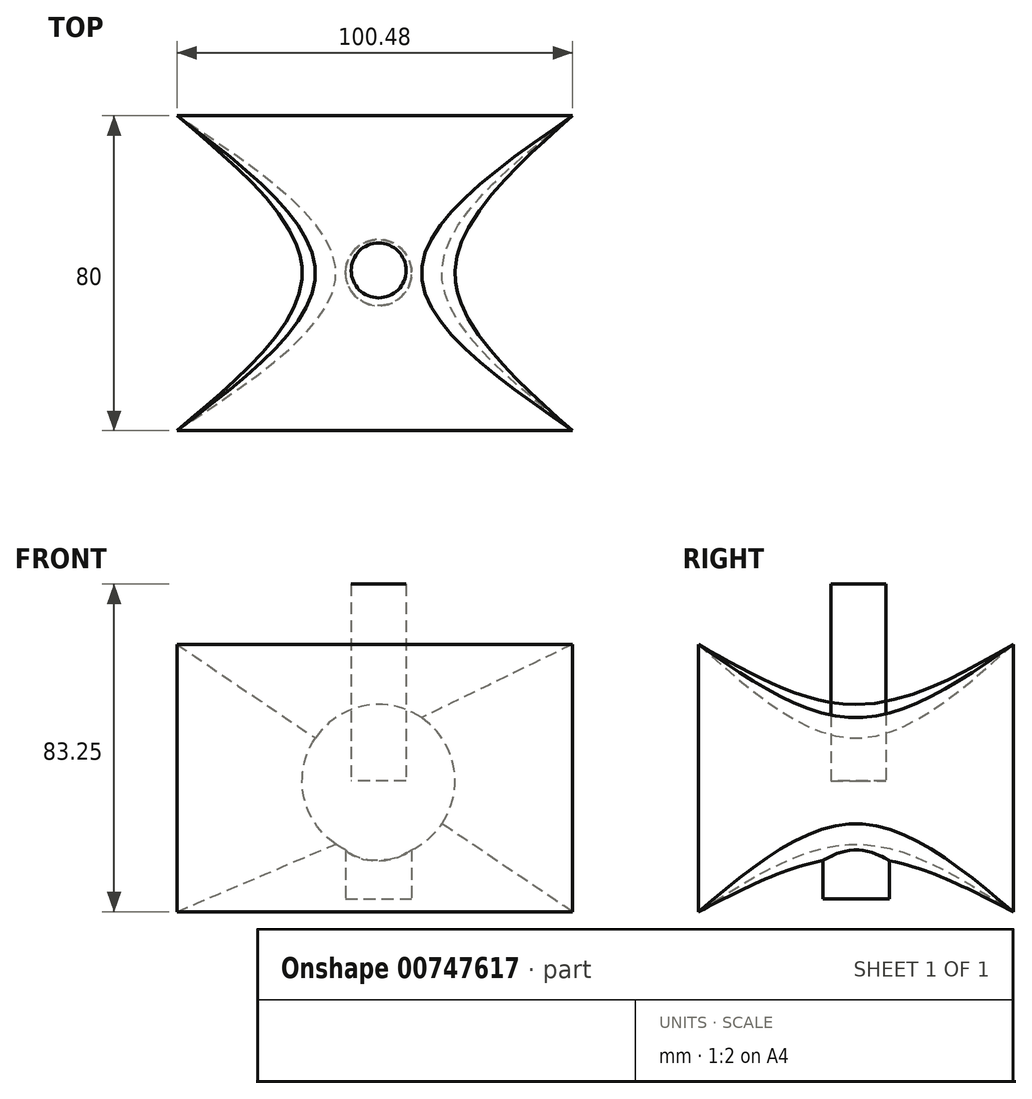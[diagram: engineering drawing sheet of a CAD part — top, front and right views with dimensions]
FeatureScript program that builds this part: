
annotation { "Feature Type Name" : "Feature", "Feature Type Description" : "" }
export const myFeature = defineFeature(function(context is Context, id is Id, definition is map)
    precondition{}
    {
        {
            var Q0;
            Q0=qCreatedBy(makeId("Front.planeOp"),FACE);
            var sketch = newSketch(context, id + "F0", { "sketchPlane" : qUnion([Q0])});
            skLineSegment(sketch, "E0.bottom", {"start": v(-51.24, 34.68) * mm, "end": v(49.24, 34.68) * mm});
            skLineSegment(sketch, "E0.top", {"start": v(-51.24, -33.25) * mm, "end": v(49.24, -33.25) * mm});
            skLineSegment(sketch, "E0.left", {"start": v(-51.24, 34.68) * mm, "end": v(-51.24, -33.25) * mm});
            skLineSegment(sketch, "E0.right", {"start": v(49.24, 34.68) * mm, "end": v(49.24, -33.25) * mm});
            skSolve(sketch);
        }
        {
            var Q0;
            Q0=qCreatedBy(makeId("Front.planeOp"),FACE);
            cPlane(context, id + "F1", {"entities" : qUnion([Q0]), "cplaneType" : CPlaneType.OFFSET, "offset" : 40 * mm, "oppositeDirection" : true, "width" : 150 * mm, "height" : 150 * mm});
        }
        {
            var Q0;
            Q0=qCreatedBy(makeId("Front.planeOp"),FACE);
            cPlane(context, id + "F2", {"entities" : qUnion([Q0]), "cplaneType" : CPlaneType.OFFSET, "offset" : 80 * mm, "oppositeDirection" : true, "width" : 150 * mm, "height" : 150 * mm});
        }
        {
            var Q0;
            Q0=qCreatedBy(id+"F1.planeOp",FACE);
            var sketch = newSketch(context, id + "F3", { "sketchPlane" : qUnion([Q0])});
            skCircle(sketch, "E1", {"center": v(0, 0) * mm, "radius": 19.4 * mm});
            skSolve(sketch);
        }
        {
            var Q0;
            Q0=qCreatedBy(id+"F2.planeOp",FACE);
            var sketch = newSketch(context, id + "F4", { "sketchPlane" : qUnion([Q0])});
            skLineSegment(sketch, "E2.bottom", {"start": v(-51.24, -33.25) * mm, "end": v(49.24, -33.25) * mm});
            skLineSegment(sketch, "E2.top", {"start": v(-51.24, 34.68) * mm, "end": v(49.24, 34.68) * mm});
            skLineSegment(sketch, "E2.left", {"start": v(-51.24, -33.25) * mm, "end": v(-51.24, 34.68) * mm});
            skLineSegment(sketch, "E2.right", {"start": v(49.24, -33.25) * mm, "end": v(49.24, 34.68) * mm});
            skSolve(sketch);
        }
        {
            var Q0;
            Q0=makeQuery(id+"F0.imprint","IMPRINT",FACE,{"disambiguationData":[TD([[makeQuery(id+"F0.imprint","IMPRINT",EDGE,{"derivedFrom":sQuery(id+"F0.wireOp",EDGE,"E0.bottom")}),-1.0]])]});
            var Q1;
            Q1=makeQuery(id+"F3.imprint","IMPRINT",FACE,{"disambiguationData":[TD([[makeQuery(id+"F3.imprint","IMPRINT",EDGE,{"derivedFrom":sQuery(id+"F3.wireOp",EDGE,"E1")}),1.0]])]});
            var Q2;
            Q2=makeQuery(id+"F4.imprint","IMPRINT",FACE,{"disambiguationData":[TD([[makeQuery(id+"F4.imprint","IMPRINT",EDGE,{"derivedFrom":sQuery(id+"F4.wireOp",EDGE,"E2.bottom")}),1.0]])]});
            loft(context, id + "F5", {"sheetProfilesArray" : [{ "sheetProfileEntities" : qUnion([Q0]) }, { "sheetProfileEntities" : qUnion([Q1]) }, { "sheetProfileEntities" : qUnion([Q2]) }]});
        }
        {
            var Q0;
            Q0=qCreatedBy(makeId("Top.planeOp"),FACE);
            var sketch = newSketch(context, id + "F6", { "sketchPlane" : qUnion([Q0])});
            skCircle(sketch, "E3", {"center": v(0, 40.7) * mm, "radius": 6.97 * mm});
            skSolve(sketch);
        }
        {
            var Q0;
            Q0 = qSketchRegion(id + "F6", true);
            extrude(context, id + "F7", {"entities" : qUnion([Q0]), "depth" : 50 * mm, "offsetDistance" : 25 * mm});
        }
        {
            var Q0;
            Q0=qCreatedBy(makeId("Top.planeOp"),FACE);
            cPlane(context, id + "F8", {"entities" : qUnion([Q0]), "cplaneType" : CPlaneType.OFFSET, "offset" : 30 * mm, "oppositeDirection" : true, "width" : 150 * mm, "height" : 150 * mm});
        }
        {
            var Q0;
            Q0=qCreatedBy(id+"F8.planeOp",FACE);
            var sketch = newSketch(context, id + "F9", { "sketchPlane" : qUnion([Q0])});
            skCircle(sketch, "E4", {"center": v(0, 40.12) * mm, "radius": 8.42 * mm});
            skSolve(sketch);
        }
        {
            var Q0;
            Q0=makeQuery(id+"F9.imprint","IMPRINT",FACE,{"disambiguationData":[TD([[makeQuery(id+"F9.imprint","IMPRINT",EDGE,{"derivedFrom":sQuery(id+"F9.wireOp",EDGE,"E4")}),1.0]])]});
            var Q1;
            Q1=sQuery(id+"F9.wireOp",EDGE,"E4");
            extrude(context, id + "F10", {"entities" : qUnion([Q0]), "operationType" : NewBodyOperationType.ADD, "surfaceEntities" : qUnion([Q1]), "endBound" : BoundingType.UP_TO_NEXT, "depth" : 25 * mm, "offsetDistance" : 25 * mm});
        }
    });
